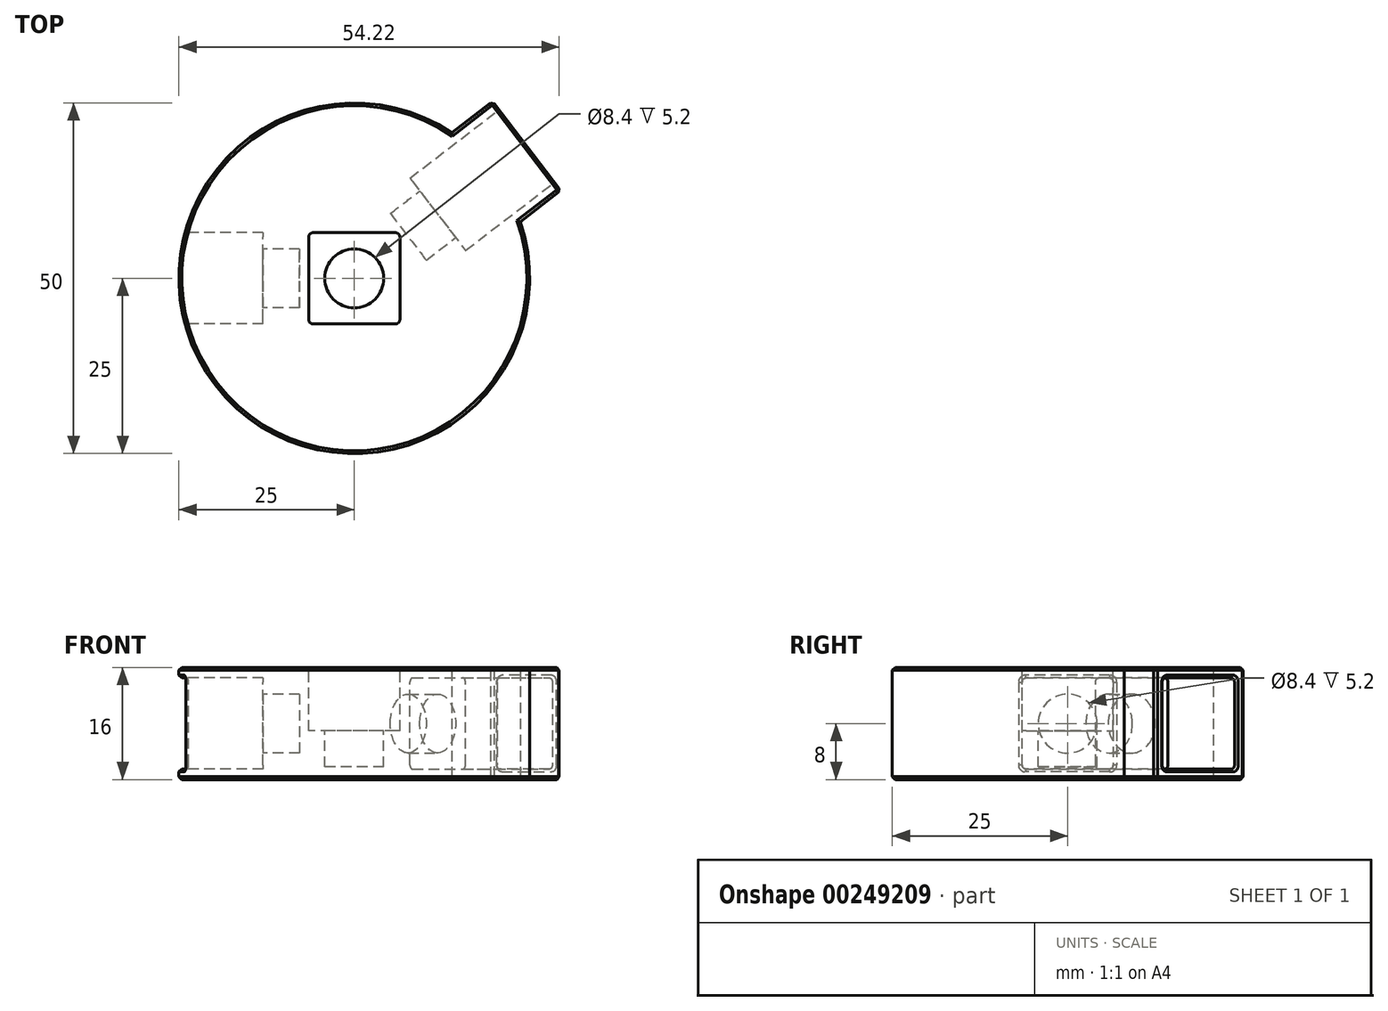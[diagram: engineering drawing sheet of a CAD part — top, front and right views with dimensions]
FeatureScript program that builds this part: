
annotation { "Feature Type Name" : "Feature", "Feature Type Description" : "" }
export const myFeature = defineFeature(function(context is Context, id is Id, definition is map)
    precondition{}
    {
        {
            var Q0;
            Q0=qCreatedBy(makeId("Top.planeOp"),FACE);
            var sketch = newSketch(context, id + "F0", { "sketchPlane" : qUnion([Q0])});
            skCircle(sketch, "E0", {"center": v(0, 0) * mm, "radius": 25 * mm});
            skSolve(sketch);
        }
        {
            var Q0;
            Q0 = qSketchRegion(id + "F0", true);
            extrude(context, id + "F1", {"entities" : qUnion([Q0]), "depth" : 16 * mm});
        }
        {
            var Q0;
            Q0=makeQuery(id+"F1.opExtrude","CAP_FACE",FACE,{"disambiguationData":[OSD([sQuery(id+"F0.wireOp",EDGE,"E0")])],"isStart":false});
            var sketch = newSketch(context, id + "F2", { "sketchPlane" : qUnion([Q0])});
            skLineSegment(sketch, "E1", {"start": v(0, 0) * mm, "end": v(19.83, 15.22) * mm});
            skLineSegment(sketch, "E2.0", {"start": v(3.96, -5.16) * mm, "end": v(23.8, 10.06) * mm});
            skLineSegment(sketch, "E3.0", {"start": v(-3.96, 5.16) * mm, "end": v(15.88, 20.38) * mm});
            skLineSegment(sketch, "E4", {"start": v(7.94, 14.29) * mm, "end": v(15.86, 3.97) * mm});
            skLineSegment(sketch, "E5", {"start": v(15.88, 20.38) * mm, "end": v(24.01, 20.38) * mm});
            skLineSegment(sketch, "E6", {"start": v(24.01, 20.38) * mm, "end": v(23.8, 10.06) * mm});
            skSolve(sketch);
        }
        {
            var Q0;
            Q0 = qSketchRegion(id + "F2", true);
            extrude(context, id + "F3", {"entities" : qUnion([Q0]), "operationType" : NewBodyOperationType.REMOVE, "oppositeDirection" : true, "depth" : (16 - 1.5) * mm, "hasSecondDirection" : true, "secondDirectionOppositeDirection" : true, "secondDirectionDepth" : 1.5 * mm});
        }
        {
            var Q0;
            Q0=makeQuery(id+"F1.opExtrude","CAP_FACE",FACE,{"disambiguationData":[OSD([sQuery(id+"F0.wireOp",EDGE,"E0")])],"isStart":false});
            var sketch = newSketch(context, id + "F4", { "sketchPlane" : qUnion([Q0])});
            skLineSegment(sketch, "E7.bottom", {"start": v(6.5, -6.5) * mm, "end": v(-6.5, -6.5) * mm});
            skLineSegment(sketch, "E7.top", {"start": v(6.5, 6.5) * mm, "end": v(-6.5, 6.5) * mm});
            skLineSegment(sketch, "E7.left", {"start": v(6.5, -6.5) * mm, "end": v(6.5, 6.5) * mm});
            skLineSegment(sketch, "E7.right", {"start": v(-6.5, -6.5) * mm, "end": v(-6.5, 6.5) * mm});
            skPoint(sketch, "E7.middle", {"position": v(0, 0) * mm});
            skSolve(sketch);
        }
        {
            var Q0;
            Q0 = qSketchRegion(id + "F4", true);
            extrude(context, id + "F5", {"entities" : qUnion([Q0]), "operationType" : NewBodyOperationType.REMOVE, "oppositeDirection" : true, "depth" : 9 * mm});
        }
        {
            var Q0;
            Q0=makeQuery(id+"F3.boolean.opBoolean","COPY",FACE,{"derivedFrom":makeQuery(id+"F3.opExtrude","SWEPT_FACE",FACE,{"disambiguationData":[OSD([sQuery(id+"F2.wireOp",EDGE,"E4")])]})});
            var sketch = newSketch(context, id + "F6", { "sketchPlane" : qUnion([Q0])});
            skCircle(sketch, "E8", {"center": v(0, 8) * mm, "radius": 4.2 * mm});
            skPoint(sketch, "E8.centerSnap0", {"position": v(0, 14.5) * mm});
            skPoint(sketch, "E8.centerSnap1", {"position": v(6.5, 8) * mm});
            skSolve(sketch);
        }
        {
            var Q0;
            Q0 = qSketchRegion(id + "F6", true);
            extrude(context, id + "F7", {"entities" : qUnion([Q0]), "operationType" : NewBodyOperationType.REMOVE, "oppositeDirection" : true, "depth" : 5.3 * mm});
        }
        {
            var Q0;
            Q0=makeQuery(id+"F5.boolean.opBoolean","COPY",FACE,{"derivedFrom":makeQuery(id+"F5.opExtrude","CAP_FACE",FACE,{"disambiguationData":[OSD([sQuery(id+"F4.wireOp",EDGE,"E7.bottom"),sQuery(id+"F4.wireOp",EDGE,"E7.top"),sQuery(id+"F4.wireOp",EDGE,"E7.left"),sQuery(id+"F4.wireOp",EDGE,"E7.right")])],"isStart":false})});
            var sketch = newSketch(context, id + "F8", { "sketchPlane" : qUnion([Q0])});
            skCircle(sketch, "E9", {"center": v(0, 0) * mm, "radius": 4.2 * mm});
            skSolve(sketch);
        }
        {
            var Q0;
            Q0 = qSketchRegion(id + "F8", true);
            extrude(context, id + "F9", {"entities" : qUnion([Q0]), "operationType" : NewBodyOperationType.REMOVE, "oppositeDirection" : true, "depth" : 5.2 * mm});
        }
        {
            var Q0;
            Q0=makeQuery(id+"F1.opExtrude","CAP_FACE",FACE,{"disambiguationData":[OSD([sQuery(id+"F0.wireOp",EDGE,"E0")])],"isStart":false});
            var sketch = newSketch(context, id + "F10", { "sketchPlane" : qUnion([Q0])});
            skLineSegment(sketch, "E10.bottom", {"start": v(-13, -6.5) * mm, "end": v(-37, -6.5) * mm});
            skLineSegment(sketch, "E10.top", {"start": v(-13, 6.5) * mm, "end": v(-37, 6.5) * mm});
            skLineSegment(sketch, "E10.left", {"start": v(-13, -6.5) * mm, "end": v(-13, 6.5) * mm});
            skLineSegment(sketch, "E10.right", {"start": v(-37, -6.5) * mm, "end": v(-37, 6.5) * mm});
            skPoint(sketch, "E10.middle", {"position": v(-25, 0) * mm});
            skSolve(sketch);
        }
        {
            var Q0;
            Q0 = qSketchRegion(id + "F10", true);
            extrude(context, id + "F11", {"entities" : qUnion([Q0]), "operationType" : NewBodyOperationType.REMOVE, "oppositeDirection" : true, "depth" : (16 - 1.5) * mm, "hasSecondDirection" : true, "secondDirectionOppositeDirection" : true, "secondDirectionDepth" : 1.5 * mm});
        }
        {
            var Q0;
            Q0=makeQuery(id+"F11.boolean.opBoolean","COPY",FACE,{"derivedFrom":makeQuery(id+"F11.opExtrude","SWEPT_FACE",FACE,{"disambiguationData":[OSD([sQuery(id+"F10.wireOp",EDGE,"E10.left")])]})});
            var sketch = newSketch(context, id + "F12", { "sketchPlane" : qUnion([Q0])});
            skCircle(sketch, "E11", {"center": v(0, 8) * mm, "radius": 4.2 * mm});
            skPoint(sketch, "E11.centerSnap0", {"position": v(-6.5, 8) * mm});
            skPoint(sketch, "E11.centerSnap1", {"position": v(0, 1.5) * mm});
            skSolve(sketch);
        }
        {
            var Q0;
            Q0 = qSketchRegion(id + "F12", true);
            extrude(context, id + "F13", {"entities" : qUnion([Q0]), "operationType" : NewBodyOperationType.REMOVE, "oppositeDirection" : true, "depth" : 5.2 * mm});
        }
        {
            var Q0;
            Q0=makeQuery(id+"F3.boolean.opBoolean","COPY",FACE,{"derivedFrom":makeQuery(id+"F3.opExtrude","SWEPT_FACE",FACE,{"disambiguationData":[OSD([sQuery(id+"F2.wireOp",EDGE,"E4")])]})});
            var sketch = newSketch(context, id + "F14", { "sketchPlane" : qUnion([Q0])});
            skLineSegment(sketch, "E12.bottom", {"start": v(8, 16) * mm, "end": v(-8, 16) * mm});
            skLineSegment(sketch, "E12.top", {"start": v(8, 0) * mm, "end": v(-8, 0) * mm});
            skLineSegment(sketch, "E12.left", {"start": v(8, 16) * mm, "end": v(8, 0) * mm});
            skLineSegment(sketch, "E12.right", {"start": v(-8, 16) * mm, "end": v(-8, 0) * mm});
            skPoint(sketch, "E12.middle", {"position": v(0, 8) * mm});
            skLineSegment(sketch, "E13.0", {"start": v(6.5, 1.5) * mm, "end": v(6.5, 14.5) * mm});
            skLineSegment(sketch, "E14.0.0", {"start": v(6.5, 14.5) * mm, "end": v(-6.5, 14.5) * mm});
            skLineSegment(sketch, "E14.0.1", {"start": v(-6.5, 14.5) * mm, "end": v(-6.5, 1.5) * mm});
            skLineSegment(sketch, "E14.0.2", {"start": v(-6.5, 1.5) * mm, "end": v(6.5, 1.5) * mm});
            skSolve(sketch);
        }
        {
            var Q0;
            Q0 = qSketchRegion(id + "F14", true);
            extrude(context, id + "F15", {"entities" : qUnion([Q0]), "operationType" : NewBodyOperationType.ADD, "depth" : 16 * mm});
        }
        {
            var Q0;
            {var subQ0=sQuery(id+"F14.wireOp",EDGE,"E12.left");var subQ2=sQuery(id+"F0.wireOp",EDGE,"E0");Q0=makeQuery(id+"Fh2wsw9045csCtE_1.1.F15.boolean.opBoolean","SPLIT",EDGE,{"disambiguationData":[TD([makeQuery(id+"F15.opExtrude","SWEPT_FACE",FACE,{"disambiguationData":[OSD([subQ0])]})])],"derivedFrom":makeQuery(id+"F1.opExtrude","CAP_EDGE",EDGE,{"disambiguationData":[OSD([subQ2])],"isStart":false})});}
            var Q1;
            {var subQ1=sQuery(id+"F14.wireOp",EDGE,"E12.right");var subQ2=sQuery(id+"F0.wireOp",EDGE,"E0");Q1=makeQuery(id+"Fh2wsw9045csCtE_1.1.F15.boolean.opBoolean","SPLIT",EDGE,{"disambiguationData":[TD([makeQuery(id+"F15.opExtrude","SWEPT_FACE",FACE,{"disambiguationData":[OSD([subQ1])]})])],"derivedFrom":makeQuery(id+"F1.opExtrude","CAP_EDGE",EDGE,{"disambiguationData":[OSD([subQ2])],"isStart":false})});}
            var Q2;
            {var subQ0=sQuery(id+"F14.wireOp",EDGE,"E12.left");var subQ2=sQuery(id+"F0.wireOp",EDGE,"E0");Q2=makeQuery(id+"Fh2wsw9045csCtE_1.1.F15.boolean.opBoolean","SPLIT",EDGE,{"disambiguationData":[TD([makeQuery(id+"F15.opExtrude","SWEPT_FACE",FACE,{"disambiguationData":[OSD([subQ0])]})])],"derivedFrom":makeQuery(id+"F1.opExtrude","CAP_EDGE",EDGE,{"disambiguationData":[OSD([subQ2])],"isStart":true})});}
            var Q3;
            {var subQ0=sQuery(id+"F14.wireOp",EDGE,"E12.right");var subQ1=sQuery(id+"F0.wireOp",EDGE,"E0");Q3=makeQuery(id+"Fh2wsw9045csCtE_1.1.F15.boolean.opBoolean","SPLIT",EDGE,{"disambiguationData":[TD([makeQuery(id+"F15.opExtrude","SWEPT_FACE",FACE,{"disambiguationData":[OSD([subQ0])]})])],"derivedFrom":makeQuery(id+"F1.opExtrude","CAP_EDGE",EDGE,{"disambiguationData":[OSD([subQ1])],"isStart":true})});}
            var Q4;
            Q4=makeQuery(id+"Fh2wsw9045csCtE_1.1.F15.opExtrude","SWEPT_EDGE",EDGE,{"disambiguationData":[OSD([sQuery(id+"F14.wireOp",EDGE,"E12.top"),sQuery(id+"F14.wireOp",EDGE,"E12.left")])]});
            var Q5;
            Q5=makeQuery(id+"Fh2wsw9045csCtE_1.1.F15.opExtrude","SWEPT_EDGE",EDGE,{"disambiguationData":[OSD([sQuery(id+"F14.wireOp",EDGE,"E12.bottom"),sQuery(id+"F14.wireOp",EDGE,"E12.left")])]});
            var Q6;
            Q6=makeQuery(id+"Fh2wsw9045csCtE_1.1.F15.opExtrude","SWEPT_EDGE",EDGE,{"disambiguationData":[OSD([sQuery(id+"F14.wireOp",EDGE,"E12.bottom"),sQuery(id+"F14.wireOp",EDGE,"E12.right")])]});
            var Q7;
            Q7=makeQuery(id+"Fh2wsw9045csCtE_1.1.F15.opExtrude","SWEPT_EDGE",EDGE,{"disambiguationData":[OSD([sQuery(id+"F14.wireOp",EDGE,"E12.top"),sQuery(id+"F14.wireOp",EDGE,"E12.right")])]});
            var Q8;
            Q8=makeQuery(id+"F15.opExtrude","SWEPT_EDGE",EDGE,{"disambiguationData":[OSD([sQuery(id+"F14.wireOp",EDGE,"E12.bottom"),sQuery(id+"F14.wireOp",EDGE,"E12.left")])]});
            var Q9;
            Q9=makeQuery(id+"F15.opExtrude","SWEPT_EDGE",EDGE,{"disambiguationData":[OSD([sQuery(id+"F14.wireOp",EDGE,"E12.bottom"),sQuery(id+"F14.wireOp",EDGE,"E12.right")])]});
            var Q10;
            Q10=makeQuery(id+"F15.opExtrude","SWEPT_EDGE",EDGE,{"disambiguationData":[OSD([sQuery(id+"F14.wireOp",EDGE,"E12.top"),sQuery(id+"F14.wireOp",EDGE,"E12.right")])]});
            var Q11;
            Q11=makeQuery(id+"F15.opExtrude","SWEPT_EDGE",EDGE,{"disambiguationData":[OSD([sQuery(id+"F14.wireOp",EDGE,"E12.top"),sQuery(id+"F14.wireOp",EDGE,"E12.left")])]});
            var Q12;
            Q12=makeQuery(id+"Fh2wsw9045csCtE_1.1.F15.opExtrude","CAP_EDGE",EDGE,{"disambiguationData":[OSD([sQuery(id+"F14.wireOp",EDGE,"E12.top")])],"isStart":false});
            var Q13;
            Q13=makeQuery(id+"Fh2wsw9045csCtE_1.1.F15.opExtrude","CAP_EDGE",EDGE,{"disambiguationData":[OSD([sQuery(id+"F14.wireOp",EDGE,"E12.left")])],"isStart":false});
            var Q14;
            Q14=makeQuery(id+"Fh2wsw9045csCtE_1.1.F15.opExtrude","CAP_EDGE",EDGE,{"disambiguationData":[OSD([sQuery(id+"F14.wireOp",EDGE,"E12.bottom")])],"isStart":false});
            var Q15;
            Q15=makeQuery(id+"Fh2wsw9045csCtE_1.1.F15.opExtrude","CAP_EDGE",EDGE,{"disambiguationData":[OSD([sQuery(id+"F14.wireOp",EDGE,"E12.right")])],"isStart":false});
            var Q16;
            Q16=makeQuery(id+"F15.opExtrude","CAP_EDGE",EDGE,{"disambiguationData":[OSD([sQuery(id+"F14.wireOp",EDGE,"E12.right")])],"isStart":false});
            var Q17;
            Q17=makeQuery(id+"F15.opExtrude","CAP_EDGE",EDGE,{"disambiguationData":[OSD([sQuery(id+"F14.wireOp",EDGE,"E12.bottom")])],"isStart":false});
            var Q18;
            Q18=makeQuery(id+"F15.opExtrude","CAP_EDGE",EDGE,{"disambiguationData":[OSD([sQuery(id+"F14.wireOp",EDGE,"E12.left")])],"isStart":false});
            var Q19;
            Q19=makeQuery(id+"F15.opExtrude","CAP_EDGE",EDGE,{"disambiguationData":[OSD([sQuery(id+"F14.wireOp",EDGE,"E12.top")])],"isStart":false});
            chamfer(context, id + "F16", {"entities" : qUnion([Q0, Q1, Q2, Q3, Q4, Q5, Q6, Q7, Q8, Q9, Q10, Q11, Q12, Q13, Q14, Q15, Q16, Q17, Q18, Q19]), "width" : 0.4 * mm, "tangentPropagation" : true});
        }
        {
            var Q0;
            Q0=makeQuery(id+"F5.boolean.opBoolean","COPY",EDGE,{"derivedFrom":makeQuery(id+"F5.opExtrude","SWEPT_EDGE",EDGE,{"disambiguationData":[OSD([sQuery(id+"F4.wireOp",EDGE,"E7.top"),sQuery(id+"F4.wireOp",EDGE,"E7.right")])]})});
            var Q1;
            Q1=makeQuery(id+"F5.boolean.opBoolean","COPY",EDGE,{"derivedFrom":makeQuery(id+"F5.opExtrude","SWEPT_EDGE",EDGE,{"disambiguationData":[OSD([sQuery(id+"F4.wireOp",EDGE,"E7.bottom"),sQuery(id+"F4.wireOp",EDGE,"E7.right")])]})});
            var Q2;
            Q2=makeQuery(id+"F5.boolean.opBoolean","COPY",EDGE,{"derivedFrom":makeQuery(id+"F5.opExtrude","SWEPT_EDGE",EDGE,{"disambiguationData":[OSD([sQuery(id+"F4.wireOp",EDGE,"E7.bottom"),sQuery(id+"F4.wireOp",EDGE,"E7.left")])]})});
            var Q3;
            Q3=makeQuery(id+"F5.boolean.opBoolean","COPY",EDGE,{"derivedFrom":makeQuery(id+"F5.opExtrude","SWEPT_EDGE",EDGE,{"disambiguationData":[OSD([sQuery(id+"F4.wireOp",EDGE,"E7.top"),sQuery(id+"F4.wireOp",EDGE,"E7.left")])]})});
            var Q4;
            Q4=makeQuery(id+"FaZdXQiBh7MHjIw_1.1.F3.boolean.opBoolean","COPY",EDGE,{"derivedFrom":makeQuery(id+"FaZdXQiBh7MHjIw_1.1.F3.opExtrude","CAP_EDGE",EDGE,{"disambiguationData":[OSD([sQuery(id+"F2.wireOp",EDGE,"E3.0")])],"isStart":true})});
            var Q5;
            Q5=makeQuery(id+"FaZdXQiBh7MHjIw_1.1.F3.boolean.opBoolean","COPY",EDGE,{"derivedFrom":makeQuery(id+"FaZdXQiBh7MHjIw_1.1.F3.opExtrude","CAP_EDGE",EDGE,{"disambiguationData":[OSD([sQuery(id+"F2.wireOp",EDGE,"E2.0")])],"isStart":true})});
            var Q6;
            Q6=makeQuery(id+"F3.boolean.opBoolean","COPY",EDGE,{"derivedFrom":makeQuery(id+"F3.opExtrude","CAP_EDGE",EDGE,{"disambiguationData":[OSD([sQuery(id+"F2.wireOp",EDGE,"E2.0")])],"isStart":true})});
            var Q7;
            Q7=makeQuery(id+"F3.boolean.opBoolean","COPY",EDGE,{"derivedFrom":makeQuery(id+"F3.opExtrude","CAP_EDGE",EDGE,{"disambiguationData":[OSD([sQuery(id+"F2.wireOp",EDGE,"E3.0")])],"isStart":true})});
            var Q8;
            Q8=makeQuery(id+"F3.boolean.opBoolean","COPY",EDGE,{"derivedFrom":makeQuery(id+"F3.opExtrude","CAP_EDGE",EDGE,{"disambiguationData":[OSD([sQuery(id+"F2.wireOp",EDGE,"E3.0")])],"isStart":false})});
            var Q9;
            Q9=makeQuery(id+"F3.boolean.opBoolean","COPY",EDGE,{"derivedFrom":makeQuery(id+"F3.opExtrude","CAP_EDGE",EDGE,{"disambiguationData":[OSD([sQuery(id+"F2.wireOp",EDGE,"E2.0")])],"isStart":false})});
            var Q10;
            Q10=makeQuery(id+"FaZdXQiBh7MHjIw_1.1.F3.boolean.opBoolean","COPY",EDGE,{"derivedFrom":makeQuery(id+"FaZdXQiBh7MHjIw_1.1.F3.opExtrude","CAP_EDGE",EDGE,{"disambiguationData":[OSD([sQuery(id+"F2.wireOp",EDGE,"E2.0")])],"isStart":false})});
            var Q11;
            Q11=makeQuery(id+"FaZdXQiBh7MHjIw_1.1.F3.boolean.opBoolean","COPY",EDGE,{"derivedFrom":makeQuery(id+"FaZdXQiBh7MHjIw_1.1.F3.opExtrude","CAP_EDGE",EDGE,{"disambiguationData":[OSD([sQuery(id+"F2.wireOp",EDGE,"E3.0")])],"isStart":false})});
            var Q12;
            Q12=makeQuery(id+"F11.boolean.opBoolean","COPY",EDGE,{"derivedFrom":makeQuery(id+"F11.opExtrude","CAP_EDGE",EDGE,{"disambiguationData":[OSD([sQuery(id+"F10.wireOp",EDGE,"E10.top")])],"isStart":false})});
            var Q13;
            Q13=makeQuery(id+"F11.boolean.opBoolean","COPY",EDGE,{"derivedFrom":makeQuery(id+"F11.opExtrude","CAP_EDGE",EDGE,{"disambiguationData":[OSD([sQuery(id+"F10.wireOp",EDGE,"E10.top")])],"isStart":true})});
            var Q14;
            Q14=makeQuery(id+"F11.boolean.opBoolean","COPY",EDGE,{"derivedFrom":makeQuery(id+"F11.opExtrude","CAP_EDGE",EDGE,{"disambiguationData":[OSD([sQuery(id+"F10.wireOp",EDGE,"E10.bottom")])],"isStart":true})});
            var Q15;
            Q15=makeQuery(id+"F11.boolean.opBoolean","COPY",EDGE,{"derivedFrom":makeQuery(id+"F11.opExtrude","CAP_EDGE",EDGE,{"disambiguationData":[OSD([sQuery(id+"F10.wireOp",EDGE,"E10.bottom")])],"isStart":false})});
            fillet(context, id + "F17", {"entities" : qUnion([Q0, Q1, Q2, Q3, Q4, Q5, Q6, Q7, Q8, Q9, Q10, Q11, Q12, Q13, Q14, Q15]), "radius" : 0.6 * mm, "tangentPropagation" : true, "allowEdgeOverflow" : false});
        }
        {
            var Q0;
            Q0=makeQuery(id+"F15.opExtrude","CAP_EDGE",EDGE,{"disambiguationData":[OSD([sQuery(id+"F14.wireOp",EDGE,"E13.0")])],"isStart":false});
            var Q1;
            Q1=makeQuery(id+"Fh2wsw9045csCtE_1.1.F15.opExtrude","CAP_EDGE",EDGE,{"disambiguationData":[OSD([sQuery(id+"F14.wireOp",EDGE,"E14.0.1")])],"isStart":false});
            var Q2;
            Q2=makeQuery(id+"F5.boolean.opBoolean","COPY",EDGE,{"derivedFrom":makeQuery(id+"F5.opExtrude","CAP_EDGE",EDGE,{"disambiguationData":[OSD([sQuery(id+"F4.wireOp",EDGE,"E7.top")])],"isStart":true})});
            var Q3;
            Q3=makeQuery(id+"F11.boolean.opBoolean","INTERSECT",EDGE,{"derivedFrom":[makeQuery(id+"F1.opExtrude","SWEPT_FACE",FACE,{"disambiguationData":[OSD([sQuery(id+"F0.wireOp",EDGE,"E0")])]}),makeQuery(id+"F11.opExtrude","SWEPT_FACE",FACE,{"disambiguationData":[OSD([sQuery(id+"F10.wireOp",EDGE,"E10.top")])]})]});
            chamfer(context, id + "F18", {"entities" : qUnion([Q0, Q1, Q2, Q3]), "width" : 0.4 * mm, "tangentPropagation" : true});
        }
    });
